# Revit family: FA_ГлавнаяЗаземпляющаяШина_10_88981_EZETEK
name_source: partatom
category: Системы пожарной сигнализации
revit_build: Autodesk Revit 2017 (Build: 20170118_1100(x64)
units: mm (PartAtom-declared; Revit-internal decimal feet)

## family parameters
Всегда вертикально = Да
На основе рабочей плоскости = Нет
Общий = Нет
При загрузке вырезать с полостями = Нет
Размер круглого соединителя = Использовать радиус
Сохранять ориентацию аннотаций = Нет
Тип детали = Нормальный
Точка расчета площади = Нет

## types (1)
- ГлавнаяЗаземпляющаяШина_10_88981
    20 = Да
    ADSK_Версия Revit = 2017
    ADSK_Единица измерения = шт.
    ADSK_Завод-изготовитель = Ezetek
    ADSK_Код изделия = 88981
    ADSK_Количество = 1
    ADSK_Марка = 88981
    ADSK_Масса = 0.91
    ADSK_Масса_Текст = 0.91
    ADSK_Материал = BIMLIB_Медь_EZETEK
    ADSK_Наименование = ГЗШ 10 подключений 300х40х4 мм, медь
    ADSK_Обозначение = 88981
    ADSK_Размер_Длина = 300 мм
    L = 260 мм
    URL = https://ezetek.ru
    l = 23 мм
    Группа модели = ГЗШ и шкафы ГЗШ
    Изготовитель = Ezetek
    КолПодключений = 10
    Описание = ГЗШ 10 подключений 300х40х4 мм, медь.

Главная заземляющая шина выполнена из меди, имеет габариты 40х4 мм, закрепляется на пластиковых изоляторах. Главная заземляющая шина объединяет нулевые защитные и нулевые рабочие совмещенные проводники питающей линии; выводы контура заземления; заземляющие проводники; проводники системы уравнивания потенциалов. Для присоединения проводников используются болты и гайки из нержавеющей стали. Главная заземляющая шина рассчитана на максимальный длительный ток 630 А.

Подходит для шкафа на 300 мм.
